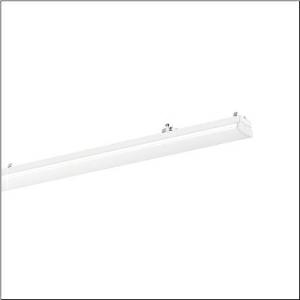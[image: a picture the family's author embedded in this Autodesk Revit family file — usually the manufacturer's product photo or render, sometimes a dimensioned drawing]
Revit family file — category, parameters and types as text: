
# Revit family: licross_r__21_recessed_opal_ho_52te1dmn4e5m_3d3a
name_source: partatom
category: Lighting Fixtures
units: mm (PartAtom-declared; Revit-internal decimal feet)

## family parameters
Cut with Voids When Loaded = No
Host = Face
Light Source = No
Part Type = Normal
Room Calculation Point = No
Round Connector Dimension = Use Diameter
Shared = No

## types (1)
- --- (1 x LED, 14660 lm, 83.1 W, 4000K)
    Apparent Load = 83 VA
    CIE Flux Codes = 44 73 91 87 100
    Color Rendering = 80
    Color Temperature = 4000K
    Default Elevation = 1800 mm
    Description = Licross® 21 recessed opal HO, luminaire insert, of sheet steel, galvanised, coil coated, white, length: 1.500mm, width: 66mm, height: 67mm, LED rated luminous flux: 14.660lm, light colour: 840, control gear: ON/OFF Multilumen, with plug, 3-pole, with phase selection, mains connection: 220..240V, AC, 50/60Hz, rated input power: 83W, internal wiring halogen-free, primary optical cover: cover, of PMMA, light emission: direct with ceiling illumination distribution, primary light characteristic: symmetric, protection rating (complete): IP54, insulation class (complete): insulation class I (protective earthing), certification: CE, ENEC, VDE, UKCA, protection symbol: D if used in an environment with non-conductive dust loads with corresponding accessories, impact resistance: IK06, permissible ambient temperature for indoor applications: -35..+30°C, corresponds to IFS (International Featured Standards) requirements for safety and quality in the food industry, reducing of maximum allowable ambient temperature of 5°C with ceiling mounting, LABS conformity tested according to VDMA 24364:2018-05, packaging unit: 1 piece
    Height = 83 mm
    Lamp = 1 x LED
    Lamp Light Flux = 14660 lm
    Lamp Power = 83.1 W
    Lamp count = 1
    Length = 1500 mm
    Luminous efficacy = 176 lm/W
    Manufacturer = Siteco
    ModVariant = No
    Model = 52TE1DMN4E5M
    Mounting Place = Ceiling
    Mounting Type = Pendant
    Number of Poles = 1
    OnlyDefault = Yes
    Power Factor = 1
    Product Name = Licross® 21 recessed opal HO
    Product group = luminaire insert | ceiling pendant
    ProductGroupID = 902
    Protection Class = Protection class I
    Protection Degree = IP 54
    RLX_Detail_Level = 1
    RLX_Emergency_Light_Flux = 0 lm
    RLX_Emergency_Type = 0
    RLX_Emergency_Type_DB = No
    RlxData = <blob elided: 24801 chars, md5=3e11e638>
    Socket = socket
    Standby Power = 0 W
    System Light Flux = 14660 lm
    System Power = 83 W
    Type Comments = factory setting: luminous flux: 100 % | (A | C | E) | 195 mA
    Type Image = l_1313666.jpg
    URL = http://relux.com
    VarID = @adj_086009
    Voltage = 0 V
    Weight = 0.00 kg
    Width = 76 mm

## geometry (parser evidence)
native form markers: Blend x4, Sweep x13
no freeform markers — native parametric forms only
